SOLIDWORKS PART (.sldprt)
format: sldprt  version: not decoded by parser v0  size: 110,080 bytes
history: native  units: mm
features: sketch x3, cut_extrude x2, material x1, extrude x1, fillet x1 (+16 scaffold rows collapsed)
feature tree (24):
  scaffold x16  (default folders/planes/origin — collapsed)
  material  "Plain Carbon Steel"
  sketch  "Sketch1"
  extrude  "Boss-Extrude1"  Depth=3.175mm
  sketch  "Sketch2"  dims[D1=2.7mm]
  cut_extrude  "Cut-Extrude1"  [1 undecoded]
  sketch  "Sketch3"  dims[D1=3.2mm]
  cut_extrude  "Cut-Extrude2"  Depth=5mm
  fillet  "Fillet1"  Radius=0.3mm
decode coverage: 5 of 7 modeling features carry decoded parameters
note: 1 parameter value undecoded
note: suppression state not decoded; provenance and decode notes live in map.json
